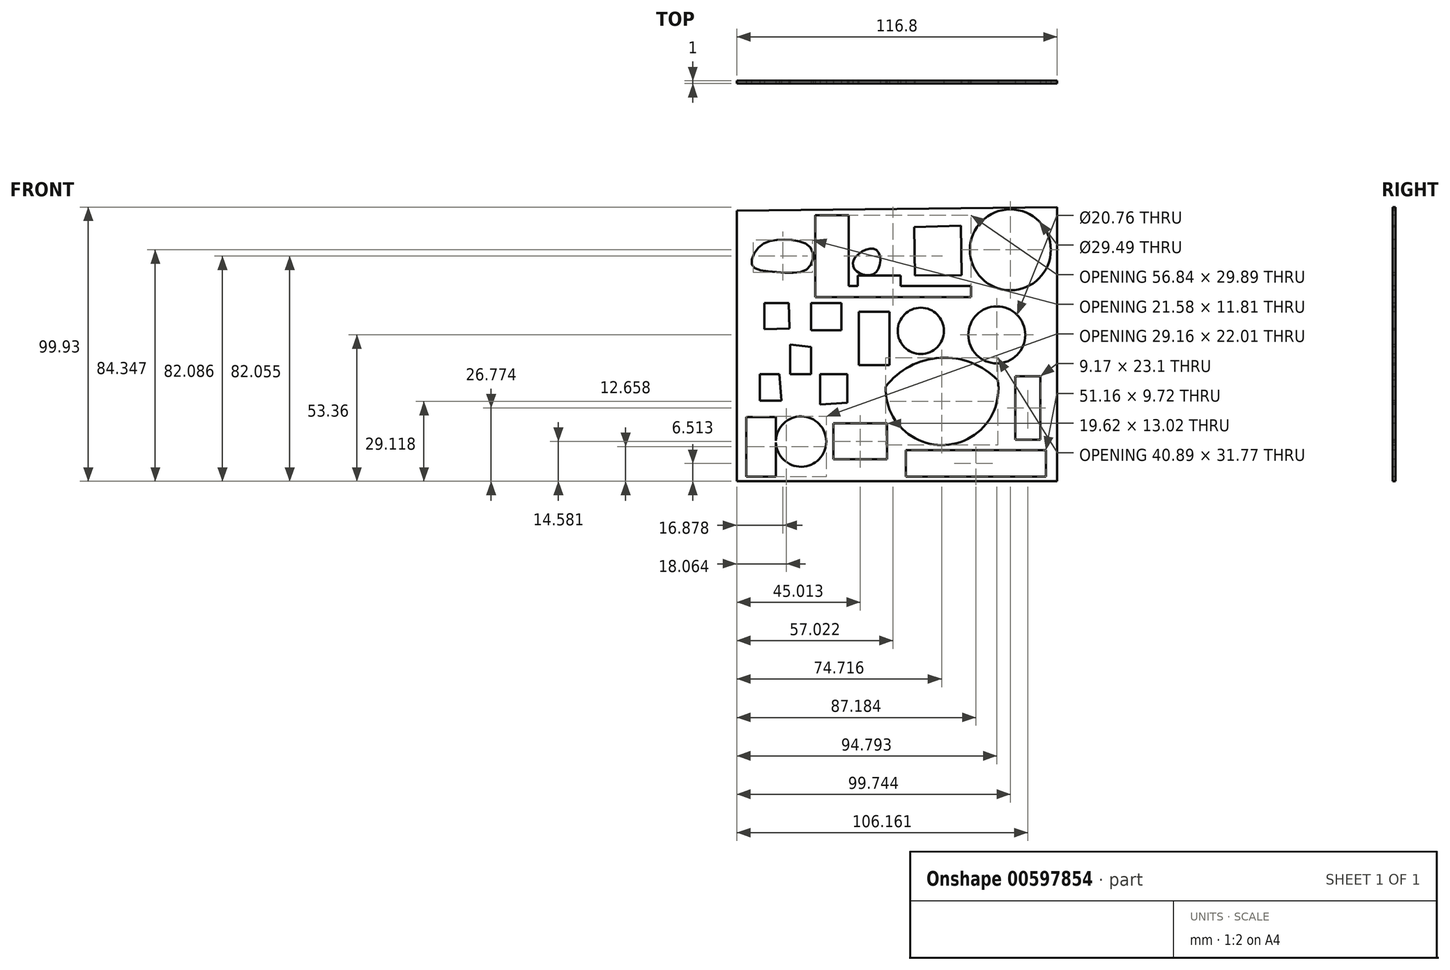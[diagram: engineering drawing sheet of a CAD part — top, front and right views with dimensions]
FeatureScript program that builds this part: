
annotation { "Feature Type Name" : "Feature", "Feature Type Description" : "" }
export const myFeature = defineFeature(function(context is Context, id is Id, definition is map)
    precondition{}
    {
        {
            var Q0;
            Q0=qCreatedBy(makeId("Front.planeOp"),FACE);
            var sketch = newSketch(context, id + "F0", { "sketchPlane" : qUnion([Q0])});
            skLineSegment(sketch, "E0", {"start": v(-50.88, 45.29) * mm, "end": v(-50.88, -53.36) * mm});
            skLineSegment(sketch, "E1", {"start": v(-50.88, -53.36) * mm, "end": v(65.92, -53.36) * mm});
            skLineSegment(sketch, "E2", {"start": v(65.92, -53.36) * mm, "end": v(65.92, 46.57) * mm});
            skLineSegment(sketch, "E3", {"start": v(65.92, 46.57) * mm, "end": v(-50.88, 45.29) * mm});
            skFitSpline(sketch, "E4", {"points": [v(-36.4, 22.92) * mm, v(-45.2, 25.3) * mm, v(-42.45, 32.27) * mm, v(-32.73, 34.65) * mm, v(-23.74, 31.54) * mm, v(-24.84, 24.2) * mm, v(-36.4, 22.92) * mm]});
            skFitSpline(sketch, "E5", {"points": [v(0, 22.92) * mm, v(-6.88, 22.92) * mm, v(-7.98, 27.87) * mm, v(0, 30.99) * mm, v(0, 22.92) * mm]});
            skLineSegment(sketch, "E6", {"start": v(13.84, 39.24) * mm, "end": v(14.04, 21.63) * mm});
            skLineSegment(sketch, "E7", {"start": v(14.04, 21.63) * mm, "end": v(31.07, 21.82) * mm});
            skLineSegment(sketch, "E8", {"start": v(31.07, 21.82) * mm, "end": v(30.88, 39.79) * mm});
            skLineSegment(sketch, "E9", {"start": v(30.88, 39.79) * mm, "end": v(13.84, 39.24) * mm});
            skLineSegment(sketch, "E10", {"start": v(-40.8, 10.45) * mm, "end": v(-40.8, 2.02) * mm});
            skLineSegment(sketch, "E11", {"start": v(-40.8, 2.02) * mm, "end": v(-31.63, 2.31) * mm});
            skLineSegment(sketch, "E12", {"start": v(-31.63, 2.31) * mm, "end": v(-31.93, 11.56) * mm});
            skLineSegment(sketch, "E13", {"start": v(-31.93, 11.56) * mm, "end": v(-40.8, 11.56) * mm});
            skLineSegment(sketch, "E14", {"start": v(-40.8, 11.56) * mm, "end": v(-40.8, 10.45) * mm});
            skLineSegment(sketch, "E15", {"start": v(-23.74, 11.56) * mm, "end": v(-23.74, 1.65) * mm});
            skLineSegment(sketch, "E16", {"start": v(-23.74, 1.65) * mm, "end": v(-12.74, 1.65) * mm});
            skLineSegment(sketch, "E17", {"start": v(-12.74, 1.65) * mm, "end": v(-12.74, 11.56) * mm});
            skLineSegment(sketch, "E18", {"start": v(-12.74, 11.56) * mm, "end": v(-23.74, 11.56) * mm});
            skLineSegment(sketch, "E19", {"start": v(-31.44, -3.48) * mm, "end": v(-31.44, -14.3) * mm});
            skLineSegment(sketch, "E20", {"start": v(-31.44, -14.3) * mm, "end": v(-23.74, -14.3) * mm});
            skLineSegment(sketch, "E21", {"start": v(-23.74, -14.3) * mm, "end": v(-23.74, -4.4) * mm});
            skLineSegment(sketch, "E22", {"start": v(-23.74, -4.4) * mm, "end": v(-31.44, -3.48) * mm});
            skLineSegment(sketch, "E23", {"start": v(-35.3, -14.3) * mm, "end": v(-42.45, -14.3) * mm});
            skLineSegment(sketch, "E24", {"start": v(-42.45, -14.3) * mm, "end": v(-42.45, -24.02) * mm});
            skLineSegment(sketch, "E25", {"start": v(-42.45, -24.02) * mm, "end": v(-34.56, -24.02) * mm});
            skLineSegment(sketch, "E26", {"start": v(-34.56, -24.02) * mm, "end": v(-35.3, -14.3) * mm});
            skLineSegment(sketch, "E27", {"start": v(-20.44, -25.3) * mm, "end": v(-20.44, -14.3) * mm});
            skLineSegment(sketch, "E28", {"start": v(-20.44, -14.3) * mm, "end": v(-10.54, -14.3) * mm});
            skLineSegment(sketch, "E29", {"start": v(-10.54, -14.3) * mm, "end": v(-10.54, -24.75) * mm});
            skLineSegment(sketch, "E30", {"start": v(-10.54, -24.75) * mm, "end": v(-20.44, -25.3) * mm});
            skCircle(sketch, "E31", {"center": v(16.23, 1.47) * mm, "radius": 8.44 * mm});
            skArc(sketch, "E32", {"start": v(3.4, -18.89) * mm, "mid": v(25.14, -40.13) * mm, "end": v(44.28, -16.5) * mm});
            skArc(sketch, "E33", {"start": v(44.28, -16.5) * mm, "mid": v(23.3, -8.36) * mm, "end": v(3.4, -18.89) * mm});
            skCircle(sketch, "E34", {"center": v(43.91, 0) * mm, "radius": 10.38 * mm});
            skCircle(sketch, "E35", {"center": v(48.86, 30.99) * mm, "radius": 14.74 * mm});
            skCircle(sketch, "E36", {"center": v(-27.41, -38.87) * mm, "radius": 9.17 * mm});
            skLineSegment(sketch, "E37.bottom", {"start": v(-47.4, -29.89) * mm, "end": v(-36.58, -29.89) * mm});
            skLineSegment(sketch, "E37.top", {"start": v(-47.4, -51.7) * mm, "end": v(-36.58, -51.7) * mm});
            skLineSegment(sketch, "E37.left", {"start": v(-47.4, -29.89) * mm, "end": v(-47.4, -51.7) * mm});
            skLineSegment(sketch, "E37.right", {"start": v(-36.58, -29.89) * mm, "end": v(-36.58, -51.7) * mm});
            skLineSegment(sketch, "E38.bottom", {"start": v(-15.68, -32.27) * mm, "end": v(3.94, -32.27) * mm});
            skLineSegment(sketch, "E38.top", {"start": v(-15.68, -45.29) * mm, "end": v(3.94, -45.29) * mm});
            skLineSegment(sketch, "E38.left", {"start": v(-15.68, -32.27) * mm, "end": v(-15.68, -45.29) * mm});
            skLineSegment(sketch, "E38.right", {"start": v(3.94, -32.27) * mm, "end": v(3.94, -45.29) * mm});
            skLineSegment(sketch, "E39.bottom", {"start": v(10.73, -41.99) * mm, "end": v(61.88, -41.99) * mm});
            skLineSegment(sketch, "E39.top", {"start": v(10.73, -51.7) * mm, "end": v(61.88, -51.7) * mm});
            skLineSegment(sketch, "E39.left", {"start": v(10.73, -41.99) * mm, "end": v(10.73, -51.7) * mm});
            skLineSegment(sketch, "E39.right", {"start": v(61.88, -41.99) * mm, "end": v(61.88, -51.7) * mm});
            skLineSegment(sketch, "E40.bottom", {"start": v(50.7, -15.03) * mm, "end": v(59.86, -15.03) * mm});
            skLineSegment(sketch, "E40.top", {"start": v(50.7, -38.14) * mm, "end": v(59.86, -38.14) * mm});
            skLineSegment(sketch, "E40.left", {"start": v(50.7, -15.03) * mm, "end": v(50.7, -38.14) * mm});
            skLineSegment(sketch, "E40.right", {"start": v(59.86, -15.03) * mm, "end": v(59.86, -38.14) * mm});
            skLineSegment(sketch, "E41.bottom", {"start": v(-6.33, 8.43) * mm, "end": v(4.86, 8.43) * mm});
            skLineSegment(sketch, "E41.top", {"start": v(-6.33, -11) * mm, "end": v(4.86, -11) * mm});
            skLineSegment(sketch, "E41.left", {"start": v(-6.33, 8.43) * mm, "end": v(-6.33, -11) * mm});
            skLineSegment(sketch, "E41.right", {"start": v(4.86, 8.43) * mm, "end": v(4.86, -11) * mm});
            skLineSegment(sketch, "E42.bottom", {"start": v(-22.28, 17.79) * mm, "end": v(34.56, 17.79) * mm});
            skLineSegment(sketch, "E42.top", {"start": v(-22.28, 13.75) * mm, "end": v(34.56, 13.75) * mm});
            skLineSegment(sketch, "E42.left", {"start": v(-22.28, 17.79) * mm, "end": v(-22.28, 13.75) * mm});
            skLineSegment(sketch, "E42.right", {"start": v(34.56, 17.79) * mm, "end": v(34.56, 13.75) * mm});
            skLineSegment(sketch, "E43.bottom", {"start": v(-22.28, 17.79) * mm, "end": v(-10, 17.79) * mm});
            skLineSegment(sketch, "E43.top", {"start": v(-22.28, 43.64) * mm, "end": v(-10, 43.64) * mm});
            skLineSegment(sketch, "E43.left", {"start": v(-22.28, 17.79) * mm, "end": v(-22.28, 43.64) * mm});
            skLineSegment(sketch, "E43.right", {"start": v(-10, 17.79) * mm, "end": v(-10, 43.64) * mm});
            skLineSegment(sketch, "E44.bottom", {"start": v(-6.7, 17.79) * mm, "end": v(8.9, 17.79) * mm});
            skLineSegment(sketch, "E44.top", {"start": v(-6.7, 21.63) * mm, "end": v(8.9, 21.63) * mm});
            skLineSegment(sketch, "E44.left", {"start": v(-6.7, 17.79) * mm, "end": v(-6.7, 21.63) * mm});
            skLineSegment(sketch, "E44.right", {"start": v(8.9, 17.79) * mm, "end": v(8.9, 21.63) * mm});
            skSolve(sketch);
        }
        {
            var Q0;
            Q0=makeQuery(id+"F0.imprint","IMPRINT",FACE,{"disambiguationData":[TD([[makeQuery(id+"F0.imprint","IMPRINT",EDGE,{"derivedFrom":sQuery(id+"F0.wireOp",EDGE,"E0")}),1.0]])]});
            extrude(context, id + "F1", {"entities" : qUnion([Q0]), "oppositeDirection" : true, "depth" : 1 * mm, "offsetDistance" : 25 * mm});
        }
    });
